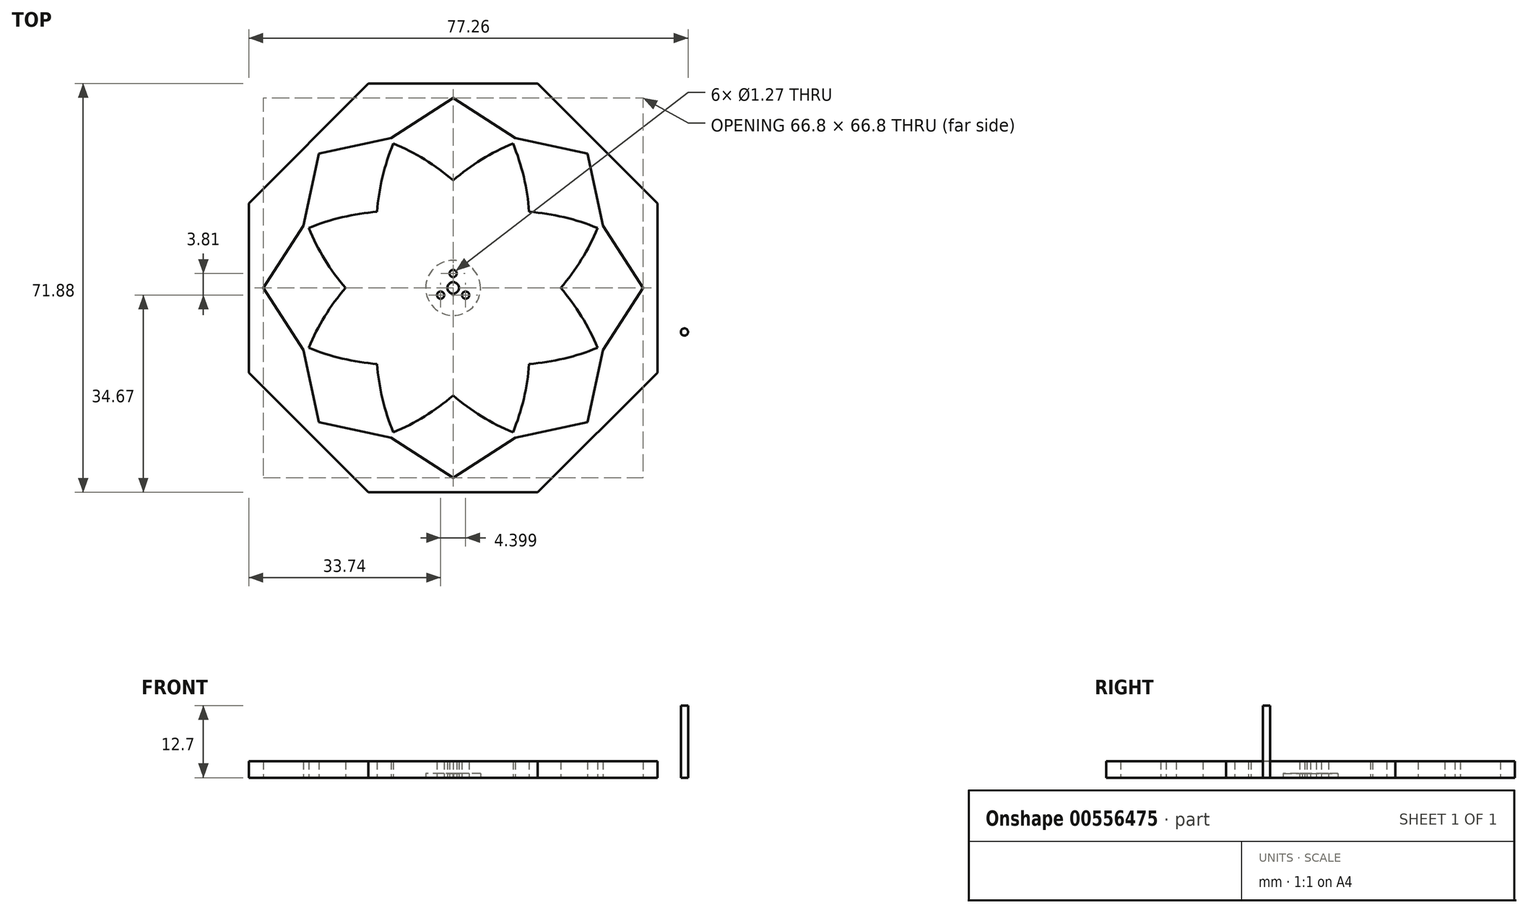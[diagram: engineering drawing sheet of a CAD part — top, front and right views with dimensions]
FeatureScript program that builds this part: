
annotation { "Feature Type Name" : "Feature", "Feature Type Description" : "" }
export const myFeature = defineFeature(function(context is Context, id is Id, definition is map)
    precondition{}
    {
        {
            var Q0;
            Q0=qCreatedBy(makeId("Top.planeOp"),FACE);
            var sketch = newSketch(context, id + "F0", { "sketchPlane" : qUnion([Q0])});
            skPoint(sketch, "E0", {"position": v(25.4, 0) * mm});
            skPoint(sketch, "E1", {"position": v(0, 0) * mm});
            skCircle(sketch, "E2.cCircle", {"center": v(0, 0) * mm, "radius": 25.4 * mm, "construction": true});
            skLineSegment(sketch, "E2.0", {"start": v(25.4, 10.52) * mm, "end": v(25.4, -10.52) * mm, "construction": true});
            skLineSegment(sketch, "E2.1", {"start": v(25.4, -10.52) * mm, "end": v(10.52, -25.4) * mm, "construction": true});
            skLineSegment(sketch, "E2.2", {"start": v(10.52, -25.4) * mm, "end": v(-10.52, -25.4) * mm, "construction": true});
            skLineSegment(sketch, "E2.3", {"start": v(-10.52, -25.4) * mm, "end": v(-25.4, -10.52) * mm, "construction": true});
            skLineSegment(sketch, "E2.4", {"start": v(-25.4, -10.52) * mm, "end": v(-25.4, 10.52) * mm, "construction": true});
            skLineSegment(sketch, "E2.5", {"start": v(-25.4, 10.52) * mm, "end": v(-10.52, 25.4) * mm, "construction": true});
            skLineSegment(sketch, "E2.6", {"start": v(-10.52, 25.4) * mm, "end": v(10.52, 25.4) * mm, "construction": true});
            skLineSegment(sketch, "E2.7", {"start": v(10.52, 25.4) * mm, "end": v(25.4, 10.52) * mm, "construction": true});
            skArc(sketch, "E3", {"start": v(10.52, -25.4) * mm, "mid": v(10.52, 4.36) * mm, "end": v(-10.52, 25.4) * mm});
            skArc(sketch, "E4", {"start": v(-10.52, 25.4) * mm, "mid": v(-10.52, -4.36) * mm, "end": v(10.52, -25.4) * mm});
            skArc(sketch, "E5", {"start": v(-10.52, -25.4) * mm, "mid": v(10.52, -4.36) * mm, "end": v(10.52, 25.4) * mm});
            skArc(sketch, "E6", {"start": v(10.52, 25.4) * mm, "mid": v(-10.52, 4.36) * mm, "end": v(-10.52, -25.4) * mm});
            skArc(sketch, "E7", {"start": v(25.4, 10.52) * mm, "mid": v(-4.36, 10.52) * mm, "end": v(-25.4, -10.52) * mm});
            skArc(sketch, "E8", {"start": v(-25.4, -10.52) * mm, "mid": v(4.36, -10.52) * mm, "end": v(25.4, 10.52) * mm});
            skArc(sketch, "E9", {"start": v(25.4, -10.52) * mm, "mid": v(4.36, 10.52) * mm, "end": v(-25.4, 10.52) * mm});
            skArc(sketch, "E10", {"start": v(-25.4, 10.52) * mm, "mid": v(-4.36, -10.52) * mm, "end": v(25.4, -10.52) * mm});
            skPoint(sketch, "E11", {"position": v(0, 2.54) * mm});
            skPoint(sketch, "E12.1.1", {"position": v(2.2, -1.27) * mm});
            skPoint(sketch, "E12.2.1", {"position": v(-2.2, -1.27) * mm});
            skLineSegment(sketch, "E12.anchor1", {"start": v(0, 0) * mm, "end": v(0, 2.54) * mm, "construction": true});
            skLineSegment(sketch, "E12.anchor2", {"start": v(0, 0) * mm, "end": v(-2.2, -1.27) * mm, "construction": true});
            skSolve(sketch);
        }
        {
            var Q0;
            {var subQ0=sQuery(id+"F0.wireOp",EDGE,"E4");var subQ1=sQuery(id+"F0.wireOp",EDGE,"E3");var subQ2=makeQuery(id+"F0.imprint","INTERSECT",VERTEX,{"disambiguationData":[OD(1.0)],"derivedFrom":[subQ1,subQ0]});Q0=makeQuery(id+"F0.imprint","IMPRINT",FACE,{"disambiguationData":[TD([[makeQuery(id+"F0.imprint","IMPRINT",EDGE,{"disambiguationData":[TD([[subQ2,-1.0]])],"derivedFrom":subQ1}),1.0]])]});}
            var Q1;
            {var subQ0=sQuery(id+"F0.wireOp",EDGE,"E8");var subQ1=sQuery(id+"F0.wireOp",EDGE,"E3");var subQ2=makeQuery(id+"F0.imprint","INTERSECT",VERTEX,{"derivedFrom":[subQ1,subQ0]});Q1=makeQuery(id+"F0.imprint","IMPRINT",FACE,{"disambiguationData":[TD([[makeQuery(id+"F0.imprint","IMPRINT",EDGE,{"disambiguationData":[TD([[subQ2,1.0]])],"derivedFrom":subQ1}),-1.0]])]});}
            var Q2;
            {var subQ0=sQuery(id+"F0.wireOp",EDGE,"E8");var subQ1=sQuery(id+"F0.wireOp",EDGE,"E3");var subQ2=makeQuery(id+"F0.imprint","INTERSECT",VERTEX,{"derivedFrom":[subQ1,subQ0]});Q2=makeQuery(id+"F0.imprint","IMPRINT",FACE,{"disambiguationData":[TD([[makeQuery(id+"F0.imprint","IMPRINT",EDGE,{"disambiguationData":[TD([[subQ2,1.0]])],"derivedFrom":subQ1}),1.0]])]});}
            var Q3;
            {var subQ0=sQuery(id+"F0.wireOp",EDGE,"E5");var subQ1=sQuery(id+"F0.wireOp",EDGE,"E4");var subQ2=makeQuery(id+"F0.imprint","INTERSECT",VERTEX,{"derivedFrom":[subQ1,subQ0]});Q3=makeQuery(id+"F0.imprint","IMPRINT",FACE,{"disambiguationData":[TD([[makeQuery(id+"F0.imprint","IMPRINT",EDGE,{"disambiguationData":[TD([[subQ2,1.0]])],"derivedFrom":subQ1}),1.0]])]});}
            var Q4;
            {var subQ0=sQuery(id+"F0.wireOp",EDGE,"E5");var subQ1=sQuery(id+"F0.wireOp",EDGE,"E4");var subQ2=makeQuery(id+"F0.imprint","INTERSECT",VERTEX,{"derivedFrom":[subQ1,subQ0]});Q4=makeQuery(id+"F0.imprint","IMPRINT",FACE,{"disambiguationData":[TD([[makeQuery(id+"F0.imprint","IMPRINT",EDGE,{"disambiguationData":[TD([[subQ2,1.0]])],"derivedFrom":subQ1}),-1.0]])]});}
            var Q5;
            {var subQ0=sQuery(id+"F0.wireOp",EDGE,"E10");var subQ1=sQuery(id+"F0.wireOp",EDGE,"E4");var subQ2=makeQuery(id+"F0.imprint","INTERSECT",VERTEX,{"derivedFrom":[subQ1,subQ0]});Q5=makeQuery(id+"F0.imprint","IMPRINT",FACE,{"disambiguationData":[TD([[makeQuery(id+"F0.imprint","IMPRINT",EDGE,{"disambiguationData":[TD([[subQ2,-1.0]])],"derivedFrom":subQ1}),-1.0]])]});}
            var Q6;
            {var subQ0=sQuery(id+"F0.wireOp",EDGE,"E8");var subQ1=sQuery(id+"F0.wireOp",EDGE,"E6");var subQ2=makeQuery(id+"F0.imprint","INTERSECT",VERTEX,{"derivedFrom":[subQ1,subQ0]});Q6=makeQuery(id+"F0.imprint","IMPRINT",FACE,{"disambiguationData":[TD([[makeQuery(id+"F0.imprint","IMPRINT",EDGE,{"disambiguationData":[TD([[subQ2,1.0]])],"derivedFrom":subQ1}),-1.0]])]});}
            var Q7;
            {var subQ0=sQuery(id+"F0.wireOp",EDGE,"E7");var subQ1=sQuery(id+"F0.wireOp",EDGE,"E4");var subQ2=makeQuery(id+"F0.imprint","INTERSECT",VERTEX,{"derivedFrom":[subQ1,subQ0]});Q7=makeQuery(id+"F0.imprint","IMPRINT",FACE,{"disambiguationData":[TD([[makeQuery(id+"F0.imprint","IMPRINT",EDGE,{"disambiguationData":[TD([[subQ2,-1.0]])],"derivedFrom":subQ1}),-1.0]])]});}
            var Q8;
            {var subQ0=sQuery(id+"F0.wireOp",EDGE,"E9");var subQ1=sQuery(id+"F0.wireOp",EDGE,"E4");var subQ2=makeQuery(id+"F0.imprint","INTERSECT",VERTEX,{"derivedFrom":[subQ1,subQ0]});Q8=makeQuery(id+"F0.imprint","IMPRINT",FACE,{"disambiguationData":[TD([[makeQuery(id+"F0.imprint","IMPRINT",EDGE,{"disambiguationData":[TD([[subQ2,-1.0]])],"derivedFrom":subQ1}),-1.0]])]});}
            var Q9;
            {var subQ0=sQuery(id+"F0.wireOp",EDGE,"E9");var subQ1=sQuery(id+"F0.wireOp",EDGE,"E4");var subQ2=makeQuery(id+"F0.imprint","INTERSECT",VERTEX,{"derivedFrom":[subQ1,subQ0]});Q9=makeQuery(id+"F0.imprint","IMPRINT",FACE,{"disambiguationData":[TD([[makeQuery(id+"F0.imprint","IMPRINT",EDGE,{"disambiguationData":[TD([[subQ2,-1.0]])],"derivedFrom":subQ1}),1.0]])]});}
            var Q10;
            {var subQ0=sQuery(id+"F0.wireOp",EDGE,"E4");var subQ1=sQuery(id+"F0.wireOp",EDGE,"E3");var subQ2=makeQuery(id+"F0.imprint","INTERSECT",VERTEX,{"disambiguationData":[OD(0.0)],"derivedFrom":[subQ1,subQ0]});Q10=makeQuery(id+"F0.imprint","IMPRINT",FACE,{"disambiguationData":[TD([[makeQuery(id+"F0.imprint","IMPRINT",EDGE,{"disambiguationData":[TD([[subQ2,1.0]])],"derivedFrom":subQ1}),1.0]])]});}
            var Q11;
            {var subQ0=sQuery(id+"F0.wireOp",EDGE,"E6");var subQ1=sQuery(id+"F0.wireOp",EDGE,"E3");var subQ2=makeQuery(id+"F0.imprint","INTERSECT",VERTEX,{"derivedFrom":[subQ1,subQ0]});Q11=makeQuery(id+"F0.imprint","IMPRINT",FACE,{"disambiguationData":[TD([[makeQuery(id+"F0.imprint","IMPRINT",EDGE,{"disambiguationData":[TD([[subQ2,1.0]])],"derivedFrom":subQ1}),1.0]])]});}
            var Q12;
            {var subQ0=sQuery(id+"F0.wireOp",EDGE,"E6");var subQ1=sQuery(id+"F0.wireOp",EDGE,"E3");var subQ2=makeQuery(id+"F0.imprint","INTERSECT",VERTEX,{"derivedFrom":[subQ1,subQ0]});Q12=makeQuery(id+"F0.imprint","IMPRINT",FACE,{"disambiguationData":[TD([[makeQuery(id+"F0.imprint","IMPRINT",EDGE,{"disambiguationData":[TD([[subQ2,1.0]])],"derivedFrom":subQ1}),-1.0]])]});}
            var Q13;
            {var subQ0=sQuery(id+"F0.wireOp",EDGE,"E9");var subQ1=sQuery(id+"F0.wireOp",EDGE,"E3");var subQ2=makeQuery(id+"F0.imprint","INTERSECT",VERTEX,{"derivedFrom":[subQ1,subQ0]});Q13=makeQuery(id+"F0.imprint","IMPRINT",FACE,{"disambiguationData":[TD([[makeQuery(id+"F0.imprint","IMPRINT",EDGE,{"disambiguationData":[TD([[subQ2,-1.0]])],"derivedFrom":subQ1}),-1.0]])]});}
            var Q14;
            {var subQ0=sQuery(id+"F0.wireOp",EDGE,"E7");var subQ1=sQuery(id+"F0.wireOp",EDGE,"E5");var subQ2=makeQuery(id+"F0.imprint","INTERSECT",VERTEX,{"derivedFrom":[subQ1,subQ0]});Q14=makeQuery(id+"F0.imprint","IMPRINT",FACE,{"disambiguationData":[TD([[makeQuery(id+"F0.imprint","IMPRINT",EDGE,{"disambiguationData":[TD([[subQ2,1.0]])],"derivedFrom":subQ1}),-1.0]])]});}
            var Q15;
            {var subQ0=sQuery(id+"F0.wireOp",EDGE,"E8");var subQ1=sQuery(id+"F0.wireOp",EDGE,"E3");var subQ2=makeQuery(id+"F0.imprint","INTERSECT",VERTEX,{"derivedFrom":[subQ1,subQ0]});Q15=makeQuery(id+"F0.imprint","IMPRINT",FACE,{"disambiguationData":[TD([[makeQuery(id+"F0.imprint","IMPRINT",EDGE,{"disambiguationData":[TD([[subQ2,-1.0]])],"derivedFrom":subQ1}),-1.0]])]});}
            var Q16;
            {var subQ0=sQuery(id+"F0.wireOp",EDGE,"E5");var subQ1=sQuery(id+"F0.wireOp",EDGE,"E3");var subQ2=makeQuery(id+"F0.imprint","INTERSECT",VERTEX,{"derivedFrom":[subQ1,subQ0]});Q16=makeQuery(id+"F0.imprint","IMPRINT",FACE,{"disambiguationData":[TD([[makeQuery(id+"F0.imprint","IMPRINT",EDGE,{"disambiguationData":[TD([[subQ2,-1.0]])],"derivedFrom":subQ1}),-1.0]])]});}
            var Q17;
            {var subQ0=sQuery(id+"F0.wireOp",EDGE,"E8");var subQ1=sQuery(id+"F0.wireOp",EDGE,"E3");var subQ2=makeQuery(id+"F0.imprint","INTERSECT",VERTEX,{"derivedFrom":[subQ1,subQ0]});Q17=makeQuery(id+"F0.imprint","IMPRINT",FACE,{"disambiguationData":[TD([[makeQuery(id+"F0.imprint","IMPRINT",EDGE,{"disambiguationData":[TD([[subQ2,-1.0]])],"derivedFrom":subQ1}),1.0]])]});}
            var Q18;
            {var subQ0=sQuery(id+"F0.wireOp",EDGE,"E10");var subQ1=sQuery(id+"F0.wireOp",EDGE,"E5");var subQ2=makeQuery(id+"F0.imprint","INTERSECT",VERTEX,{"derivedFrom":[subQ1,subQ0]});Q18=makeQuery(id+"F0.imprint","IMPRINT",FACE,{"disambiguationData":[TD([[makeQuery(id+"F0.imprint","IMPRINT",EDGE,{"disambiguationData":[TD([[subQ2,-1.0]])],"derivedFrom":subQ1}),1.0]])]});}
            var Q19;
            {var subQ0=sQuery(id+"F0.wireOp",EDGE,"E10");var subQ1=sQuery(id+"F0.wireOp",EDGE,"E4");var subQ2=makeQuery(id+"F0.imprint","INTERSECT",VERTEX,{"derivedFrom":[subQ1,subQ0]});Q19=makeQuery(id+"F0.imprint","IMPRINT",FACE,{"disambiguationData":[TD([[makeQuery(id+"F0.imprint","IMPRINT",EDGE,{"disambiguationData":[TD([[subQ2,-1.0]])],"derivedFrom":subQ1}),1.0]])]});}
            var Q20;
            {var subQ0=sQuery(id+"F0.wireOp",EDGE,"E6");var subQ1=sQuery(id+"F0.wireOp",EDGE,"E4");var subQ2=makeQuery(id+"F0.imprint","INTERSECT",VERTEX,{"derivedFrom":[subQ1,subQ0]});Q20=makeQuery(id+"F0.imprint","IMPRINT",FACE,{"disambiguationData":[TD([[makeQuery(id+"F0.imprint","IMPRINT",EDGE,{"disambiguationData":[TD([[subQ2,-1.0]])],"derivedFrom":subQ1}),-1.0]])]});}
            var Q21;
            {var subQ0=sQuery(id+"F0.wireOp",EDGE,"E7");var subQ1=sQuery(id+"F0.wireOp",EDGE,"E4");var subQ2=makeQuery(id+"F0.imprint","INTERSECT",VERTEX,{"derivedFrom":[subQ1,subQ0]});Q21=makeQuery(id+"F0.imprint","IMPRINT",FACE,{"disambiguationData":[TD([[makeQuery(id+"F0.imprint","IMPRINT",EDGE,{"disambiguationData":[TD([[subQ2,-1.0]])],"derivedFrom":subQ1}),1.0]])]});}
            var Q22;
            {var subQ0=sQuery(id+"F0.wireOp",EDGE,"E9");var subQ1=sQuery(id+"F0.wireOp",EDGE,"E6");var subQ2=makeQuery(id+"F0.imprint","INTERSECT",VERTEX,{"derivedFrom":[subQ1,subQ0]});Q22=makeQuery(id+"F0.imprint","IMPRINT",FACE,{"disambiguationData":[TD([[makeQuery(id+"F0.imprint","IMPRINT",EDGE,{"disambiguationData":[TD([[subQ2,-1.0]])],"derivedFrom":subQ1}),1.0]])]});}
            var Q23;
            {var subQ0=sQuery(id+"F0.wireOp",EDGE,"E9");var subQ1=sQuery(id+"F0.wireOp",EDGE,"E3");var subQ2=makeQuery(id+"F0.imprint","INTERSECT",VERTEX,{"derivedFrom":[subQ1,subQ0]});Q23=makeQuery(id+"F0.imprint","IMPRINT",FACE,{"disambiguationData":[TD([[makeQuery(id+"F0.imprint","IMPRINT",EDGE,{"disambiguationData":[TD([[subQ2,-1.0]])],"derivedFrom":subQ1}),1.0]])]});}
            var Q24;
            {var subQ5=sQuery(id+"F0.wireOp",EDGE,"E5");var subQ6=sQuery(id+"F0.wireOp",EDGE,"E3");var subQ7=makeQuery(id+"F0.imprint","INTERSECT",VERTEX,{"derivedFrom":[subQ6,subQ5]});Q24=makeQuery(id+"F0.imprint","IMPRINT",FACE,{"disambiguationData":[TD([[makeQuery(id+"F0.imprint","IMPRINT",EDGE,{"disambiguationData":[TD([[subQ7,-1.0]])],"derivedFrom":subQ6}),1.0]])]});}
            extrude(context, id + "F1", {"entities" : qUnion([Q0, Q1, Q2, Q3, Q4, Q5, Q6, Q7, Q8, Q9, Q10, Q11, Q12, Q13, Q14, Q15, Q16, Q17, Q18, Q19, Q20, Q21, Q22, Q23, Q24]), "depth" : 2.92 * mm, "offsetDistance" : 25.4 * mm});
        }
        {
            var Q0;
            Q0=sQuery(id+"F0.wireOp",VERTEX,"E1");
            var Q1;
            Q1=makeQuery(id+"F1.opExtrude","SWEPT_BODY",BODY,{"disambiguationData":[OSD([sQuery(id+"F0.wireOp",EDGE,"E3"),sQuery(id+"F0.wireOp",EDGE,"E4"),sQuery(id+"F0.wireOp",EDGE,"E5"),sQuery(id+"F0.wireOp",EDGE,"E6"),sQuery(id+"F0.wireOp",EDGE,"E7"),sQuery(id+"F0.wireOp",EDGE,"E8"),sQuery(id+"F0.wireOp",EDGE,"E9"),sQuery(id+"F0.wireOp",EDGE,"E10")])]});
            hole(context, id + "F2", {"style" : HoleStyle.SIMPLE, "endStyle" : HoleEndStyle.BLIND, "oppositeDirection" : true, "holeDiameter" : 2.03 * mm, "majorDiameter" : 6.35 * mm, "holeDepth" : 12.7 * mm, "isTappedThrough" : true, "tappedDepth" : 12.7 * mm, "tapClearance" : 3, "locations" : qUnion([Q0]), "scope" : qUnion([Q1])});
        }
        {
            var Q0;
            Q0=sQuery(id+"F0.wireOp",VERTEX,"E12.1.1");
            var Q1;
            Q1=sQuery(id+"F0.wireOp",VERTEX,"E12.2.1");
            var Q2;
            Q2=sQuery(id+"F0.wireOp",VERTEX,"E11");
            var Q3;
            Q3=makeQuery(id+"F1.opExtrude","SWEPT_BODY",BODY,{"disambiguationData":[OSD([sQuery(id+"F0.wireOp",EDGE,"E3"),sQuery(id+"F0.wireOp",EDGE,"E4"),sQuery(id+"F0.wireOp",EDGE,"E5"),sQuery(id+"F0.wireOp",EDGE,"E6"),sQuery(id+"F0.wireOp",EDGE,"E7"),sQuery(id+"F0.wireOp",EDGE,"E8"),sQuery(id+"F0.wireOp",EDGE,"E9"),sQuery(id+"F0.wireOp",EDGE,"E10")])]});
            hole(context, id + "F3", {"style" : HoleStyle.SIMPLE, "endStyle" : HoleEndStyle.BLIND, "oppositeDirection" : true, "holeDiameter" : 1.27 * mm, "majorDiameter" : 6.35 * mm, "holeDepth" : 12.7 * mm, "isTappedThrough" : true, "tappedDepth" : 12.7 * mm, "tapClearance" : 3, "locations" : qUnion([Q0, Q1, Q2]), "scope" : qUnion([Q3])});
        }
        {
            var Q0;
            Q0=qCreatedBy(makeId("Top.planeOp"),FACE);
            var sketch = newSketch(context, id + "F4", { "sketchPlane" : qUnion([Q0])});
            skPoint(sketch, "E13", {"position": v(33.4, 0) * mm});
            skCircle(sketch, "E14.cCircle", {"center": v(0, 0) * mm, "radius": 33.4 * mm, "construction": true});
            skLineSegment(sketch, "E14.0", {"start": v(33.4, 13.84) * mm, "end": v(33.4, -13.84) * mm});
            skLineSegment(sketch, "E14.1", {"start": v(33.4, -13.84) * mm, "end": v(13.84, -33.4) * mm});
            skLineSegment(sketch, "E14.2", {"start": v(13.84, -33.4) * mm, "end": v(-13.84, -33.4) * mm});
            skLineSegment(sketch, "E14.3", {"start": v(-13.84, -33.4) * mm, "end": v(-33.4, -13.84) * mm});
            skLineSegment(sketch, "E14.4", {"start": v(-33.4, -13.84) * mm, "end": v(-33.4, 13.84) * mm});
            skLineSegment(sketch, "E14.5", {"start": v(-33.4, 13.84) * mm, "end": v(-13.84, 33.4) * mm});
            skLineSegment(sketch, "E14.6", {"start": v(-13.84, 33.4) * mm, "end": v(13.84, 33.4) * mm});
            skLineSegment(sketch, "E14.7", {"start": v(13.84, 33.4) * mm, "end": v(33.4, 13.84) * mm});
            skPoint(sketch, "E15", {"position": v(0, 33.4) * mm});
            skPoint(sketch, "E16", {"position": v(0, -33.4) * mm});
            skPoint(sketch, "E17", {"position": v(23.62, -23.62) * mm});
            skPoint(sketch, "E18", {"position": v(-23.62, -23.62) * mm});
            skPoint(sketch, "E19", {"position": v(-33.4, 0) * mm});
            skPoint(sketch, "E20", {"position": v(-23.62, 23.62) * mm});
            skPoint(sketch, "E21", {"position": v(23.62, 23.62) * mm});
            skPoint(sketch, "E22", {"position": v(25.4, 0) * mm});
            skCircle(sketch, "E23.cCircle", {"center": v(0, 0) * mm, "radius": 25.4 * mm, "construction": true});
            skLineSegment(sketch, "E23.0", {"start": v(25.4, 10.52) * mm, "end": v(25.4, -10.52) * mm, "construction": true});
            skLineSegment(sketch, "E23.1", {"start": v(25.4, -10.52) * mm, "end": v(10.52, -25.4) * mm, "construction": true});
            skLineSegment(sketch, "E23.2", {"start": v(10.52, -25.4) * mm, "end": v(-10.52, -25.4) * mm, "construction": true});
            skLineSegment(sketch, "E23.3", {"start": v(-10.52, -25.4) * mm, "end": v(-25.4, -10.52) * mm, "construction": true});
            skLineSegment(sketch, "E23.4", {"start": v(-25.4, -10.52) * mm, "end": v(-25.4, 10.52) * mm, "construction": true});
            skLineSegment(sketch, "E23.5", {"start": v(-25.4, 10.52) * mm, "end": v(-10.52, 25.4) * mm, "construction": true});
            skLineSegment(sketch, "E23.6", {"start": v(-10.52, 25.4) * mm, "end": v(10.52, 25.4) * mm, "construction": true});
            skLineSegment(sketch, "E23.7", {"start": v(10.52, 25.4) * mm, "end": v(25.4, 10.52) * mm, "construction": true});
            skLineSegment(sketch, "E24", {"start": v(-10.52, 25.4) * mm, "end": v(-13.84, 33.4) * mm, "construction": true});
            skLineSegment(sketch, "E25", {"start": v(10.52, 25.4) * mm, "end": v(13.84, 33.4) * mm, "construction": true});
            skLineSegment(sketch, "E26", {"start": v(25.4, 10.52) * mm, "end": v(33.4, 13.84) * mm, "construction": true});
            skLineSegment(sketch, "E27", {"start": v(25.4, -10.52) * mm, "end": v(33.4, -13.84) * mm, "construction": true});
            skLineSegment(sketch, "E28", {"start": v(13.84, -33.4) * mm, "end": v(10.52, -25.4) * mm, "construction": true});
            skLineSegment(sketch, "E29", {"start": v(-13.84, -33.4) * mm, "end": v(-10.52, -25.4) * mm, "construction": true});
            skLineSegment(sketch, "E30", {"start": v(-33.4, -13.84) * mm, "end": v(-25.4, -10.52) * mm, "construction": true});
            skLineSegment(sketch, "E31", {"start": v(-33.4, 13.84) * mm, "end": v(-25.4, 10.52) * mm, "construction": true});
            skPoint(sketch, "E32", {"position": v(-10.92, 26.36) * mm});
            skLineSegment(sketch, "E33", {"start": v(-23.62, 23.62) * mm, "end": v(-10.92, 26.36) * mm});
            skLineSegment(sketch, "E34", {"start": v(0, 33.4) * mm, "end": v(-10.92, 26.36) * mm});
            skLineSegment(sketch, "E35", {"start": v(0, 33.4) * mm, "end": v(0, -33.4) * mm, "construction": true});
            skLineSegment(sketch, "E36", {"start": v(-33.4, 0) * mm, "end": v(33.4, 0) * mm, "construction": true});
            skPoint(sketch, "E37", {"position": v(-26.36, 10.92) * mm});
            skLineSegment(sketch, "E38.MirrorCS", {"start": v(0, 33.4) * mm, "end": v(10.92, 26.36) * mm});
            skLineSegment(sketch, "E39.MirrorCS", {"start": v(23.62, 23.62) * mm, "end": v(10.92, 26.36) * mm});
            skLineSegment(sketch, "E40", {"start": v(-23.62, 23.62) * mm, "end": v(-26.36, 10.92) * mm});
            skLineSegment(sketch, "E41", {"start": v(-33.4, 0) * mm, "end": v(-26.36, 10.92) * mm});
            skLineSegment(sketch, "E42.MirrorCS", {"start": v(23.62, 23.62) * mm, "end": v(26.36, 10.92) * mm});
            skLineSegment(sketch, "E43.MirrorCS", {"start": v(33.4, 0) * mm, "end": v(26.36, 10.92) * mm});
            skLineSegment(sketch, "E44.MirrorCS", {"start": v(33.4, 0) * mm, "end": v(26.36, -10.92) * mm});
            skLineSegment(sketch, "E45.MirrorCS", {"start": v(23.62, -23.62) * mm, "end": v(26.36, -10.92) * mm});
            skLineSegment(sketch, "E46.MirrorCS", {"start": v(23.62, -23.62) * mm, "end": v(10.92, -26.36) * mm});
            skLineSegment(sketch, "E47.MirrorCS", {"start": v(0, -33.4) * mm, "end": v(10.92, -26.36) * mm});
            skLineSegment(sketch, "E48.MirrorCS", {"start": v(-23.62, -23.62) * mm, "end": v(-10.92, -26.36) * mm});
            skLineSegment(sketch, "E49.MirrorCS", {"start": v(-23.62, -23.62) * mm, "end": v(-26.36, -10.92) * mm});
            skLineSegment(sketch, "E50.MirrorCS", {"start": v(-33.4, 0) * mm, "end": v(-26.36, -10.92) * mm});
            skLineSegment(sketch, "E51.MirrorCS", {"start": v(0, -33.4) * mm, "end": v(-10.92, -26.36) * mm});
            skPoint(sketch, "E52", {"position": v(35.94, 0) * mm});
            skCircle(sketch, "E53.cCircle", {"center": v(0, 0) * mm, "radius": 35.94 * mm, "construction": true});
            skLineSegment(sketch, "E53.0", {"start": v(35.94, 14.89) * mm, "end": v(35.94, -14.89) * mm});
            skLineSegment(sketch, "E53.1", {"start": v(35.94, -14.89) * mm, "end": v(14.89, -35.94) * mm});
            skLineSegment(sketch, "E53.2", {"start": v(14.89, -35.94) * mm, "end": v(-14.89, -35.94) * mm});
            skLineSegment(sketch, "E53.3", {"start": v(-14.89, -35.94) * mm, "end": v(-35.94, -14.89) * mm});
            skLineSegment(sketch, "E53.4", {"start": v(-35.94, -14.89) * mm, "end": v(-35.94, 14.89) * mm});
            skLineSegment(sketch, "E53.5", {"start": v(-35.94, 14.89) * mm, "end": v(-14.89, 35.94) * mm});
            skLineSegment(sketch, "E53.6", {"start": v(-14.89, 35.94) * mm, "end": v(14.89, 35.94) * mm});
            skLineSegment(sketch, "E53.7", {"start": v(14.89, 35.94) * mm, "end": v(35.94, 14.89) * mm});
            skSolve(sketch);
        }
        {
            var Q0;
            {var subQ0=sQuery(id+"F4.wireOp",EDGE,"E33");Q0=makeQuery(id+"F4.imprint","IMPRINT",FACE,{"disambiguationData":[TD([[makeQuery(id+"F4.imprint","IMPRINT",EDGE,{"derivedFrom":subQ0}),1.0]])]});}
            var Q1;
            Q1=makeQuery(id+"F4.imprint","IMPRINT",FACE,{"disambiguationData":[TD([[makeQuery(id+"F4.imprint","IMPRINT",EDGE,{"derivedFrom":sQuery(id+"F4.wireOp",EDGE,"E53.0")}),-1.0]])]});
            var Q2;
            {var subQ0=sQuery(id+"F4.wireOp",EDGE,"E38.MirrorCS");Q2=makeQuery(id+"F4.imprint","IMPRINT",FACE,{"disambiguationData":[TD([[makeQuery(id+"F4.imprint","IMPRINT",EDGE,{"derivedFrom":subQ0}),1.0]])]});}
            var Q3;
            {var subQ4=sQuery(id+"F4.wireOp",EDGE,"E42.MirrorCS");Q3=makeQuery(id+"F4.imprint","IMPRINT",FACE,{"disambiguationData":[TD([[makeQuery(id+"F4.imprint","IMPRINT",EDGE,{"derivedFrom":subQ4}),1.0]])]});}
            var Q4;
            {var subQ3=sQuery(id+"F4.wireOp",EDGE,"E44.MirrorCS");Q4=makeQuery(id+"F4.imprint","IMPRINT",FACE,{"disambiguationData":[TD([[makeQuery(id+"F4.imprint","IMPRINT",EDGE,{"derivedFrom":subQ3}),1.0]])]});}
            var Q5;
            {var subQ4=sQuery(id+"F4.wireOp",EDGE,"E40");Q5=makeQuery(id+"F4.imprint","IMPRINT",FACE,{"disambiguationData":[TD([[makeQuery(id+"F4.imprint","IMPRINT",EDGE,{"derivedFrom":subQ4}),-1.0]])]});}
            var Q6;
            {var subQ4=sQuery(id+"F4.wireOp",EDGE,"E48.MirrorCS");Q6=makeQuery(id+"F4.imprint","IMPRINT",FACE,{"disambiguationData":[TD([[makeQuery(id+"F4.imprint","IMPRINT",EDGE,{"derivedFrom":subQ4}),-1.0]])]});}
            var Q7;
            {var subQ0=sQuery(id+"F4.wireOp",EDGE,"E49.MirrorCS");Q7=makeQuery(id+"F4.imprint","IMPRINT",FACE,{"disambiguationData":[TD([[makeQuery(id+"F4.imprint","IMPRINT",EDGE,{"derivedFrom":subQ0}),1.0]])]});}
            var Q8;
            {var subQ3=sQuery(id+"F4.wireOp",EDGE,"E46.MirrorCS");Q8=makeQuery(id+"F4.imprint","IMPRINT",FACE,{"disambiguationData":[TD([[makeQuery(id+"F4.imprint","IMPRINT",EDGE,{"derivedFrom":subQ3}),1.0]])]});}
            extrude(context, id + "F5", {"entities" : qUnion([Q0, Q1, Q2, Q3, Q4, Q5, Q6, Q7, Q8]), "depth" : 2.92 * mm, "offsetDistance" : 25.4 * mm});
        }
        {
            var Q0;
            Q0=qCreatedBy(makeId("Top.planeOp"),FACE);
            var sketch = newSketch(context, id + "F6", { "sketchPlane" : qUnion([Q0])});
            skPoint(sketch, "E54", {"position": v(1.02, 0) * mm});
            skPoint(sketch, "E55", {"position": v(4.83, 0) * mm});
            skCircle(sketch, "E56", {"center": v(0, 0) * mm, "radius": 4.83 * mm});
            skPoint(sketch, "E57", {"position": v(2.2, -1.27) * mm});
            skPoint(sketch, "E58", {"position": v(0, 2.54) * mm});
            skPoint(sketch, "E59", {"position": v(-2.2, -1.27) * mm});
            skCircle(sketch, "E60", {"center": v(0, 2.54) * mm, "radius": 0.64 * mm});
            skCircle(sketch, "E61", {"center": v(-2.2, -1.27) * mm, "radius": 0.64 * mm});
            skCircle(sketch, "E62", {"center": v(2.2, -1.27) * mm, "radius": 0.64 * mm});
            skCircle(sketch, "E63", {"center": v(0, 0) * mm, "radius": 1.02 * mm});
            skLineSegment(sketch, "E64", {"start": v(0, -1.02) * mm, "end": v(0, -1.4) * mm});
            skArc(sketch, "E65.0.startCap", {"start": v(-6.35, -1.02) * mm, "mid": v(0, 5.33) * mm, "end": v(6.35, -1.02) * mm});
            skArc(sketch, "E65.0.endCap", {"start": v(6.35, -1.4) * mm, "mid": v(0, -7.75) * mm, "end": v(-6.35, -1.4) * mm});
            skLineSegment(sketch, "E65.0.left", {"start": v(6.35, -1.02) * mm, "end": v(6.35, -1.4) * mm});
            skLineSegment(sketch, "E65.0.right", {"start": v(-6.35, -1.02) * mm, "end": v(-6.35, -1.4) * mm});
            skLineSegment(sketch, "E66.0", {"start": v(0.06, -1.01) * mm, "end": v(0.06, -1.4) * mm});
            skLineSegment(sketch, "E67.0", {"start": v(-0.06, -1.01) * mm, "end": v(-0.06, -1.4) * mm});
            skArc(sketch, "E68", {"start": v(-0.06, -1.4) * mm, "mid": v(0, -1.46) * mm, "end": v(0.06, -1.4) * mm});
            skSolve(sketch);
        }
        {
            var Q0;
            Q0=makeQuery(id+"F6.imprint","IMPRINT",FACE,{"disambiguationData":[TD([[makeQuery(id+"F6.imprint","IMPRINT",EDGE,{"derivedFrom":sQuery(id+"F6.wireOp",EDGE,"E56")}),1.0]])]});
            extrude(context, id + "F7", {"entities" : qUnion([Q0]), "depth" : 0.76 * mm, "offsetDistance" : 25.4 * mm});
        }
        {
            var Q0;
            Q0=qCreatedBy(makeId("Top.planeOp"),FACE);
            var sketch = newSketch(context, id + "F8", { "sketchPlane" : qUnion([Q0])});
            skPoint(sketch, "E69", {"position": v(40.69, -7.76) * mm});
            skCircle(sketch, "E70", {"center": v(40.69, -7.76) * mm, "radius": 0.64 * mm});
            skSolve(sketch);
        }
        {
            var Q0;
            Q0=makeQuery(id+"F8.imprint","IMPRINT",FACE,{"disambiguationData":[TD([[makeQuery(id+"F8.imprint","IMPRINT",EDGE,{"derivedFrom":sQuery(id+"F8.wireOp",EDGE,"E70")}),1.0]])]});
            extrude(context, id + "F9", {"entities" : qUnion([Q0]), "depth" : 12.7 * mm, "offsetDistance" : 25.4 * mm});
        }
    });
